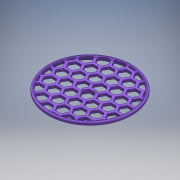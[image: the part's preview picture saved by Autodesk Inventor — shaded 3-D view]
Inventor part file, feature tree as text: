
AUTODESK INVENTOR PART (.ipt)
format: ipt  version: 2017 (Build 210142000, 142)  size: 715,264 bytes
history: native  units: mm
features: other x5, extrude x3, sketch x3, chamfer x2, reference x2, fillet x1, revolve x1
ambient origin geometry x8: Origin, YZ Plane, XZ Plane, XY Plane, X Axis, Y Axis, Z Axis, Center Point
bodies: solido (feature_tree)
feature tree (17):
  other  "Sólido1"
  extrude  "taladros"  Depth=68.5mm
  extrude  "borde"  TaperAngle=0.0deg  [1 undecoded]
  chamfer  "chaflanes interiores"  Distance=3.0mm
  extrude  "Extrusión5"  Depth=10.0mm
  chamfer  "chaflanes_pata_central"  Distance=8.0mm
  fillet  "radios exteriores"  Radius=8.660254mm
  other  "Edición directa1"
  sketch  "Boceto1"  dims[d0=70.0mm d1=68.5mm]
  reference  "Referencia1"
  reference  "Referencia2"
  sketch  "Boceto4"  dims[d3=2.0mm d4=0.0mm d30=0.0mm d31=0.0mm d34=3.0mm d35=0.0mm]
  sketch  "Boceto6"  dims[d42=8.0mm d43=10.0mm d45=10.0mm d46=80.0mm d48=10.0mm d50=8.0mm d51=8.660254mm d52=10.0mm d54=10.0mm d55=80.0mm d57=10.0mm d59=40.0mm d61=17.32mm d62=10.0mm d64=10.0mm d69=0.5mm d70=2.0mm d71=45.0deg d72=10.0mm d73=0.0mm d75=68.5mm d76=1.0mm d77=2.0mm d78=45.0deg d79=1.0mm d80=62.009301mm d81=64.5mm d82=180.0deg]
  other  "<userpath>\Dropbox\3D_print\diseños_PROPIOS\soap_box\conjunto_v2.iam"
  other  "conjunto_v2.iam"
  other  "box:1"
  revolve  "Girar1"  [1 undecoded]
note: 2 required parameter values undecoded (feature->parameter linkage not recoverable at this tier; creation-order binding heuristic only, values carry confidence <= 0.55)